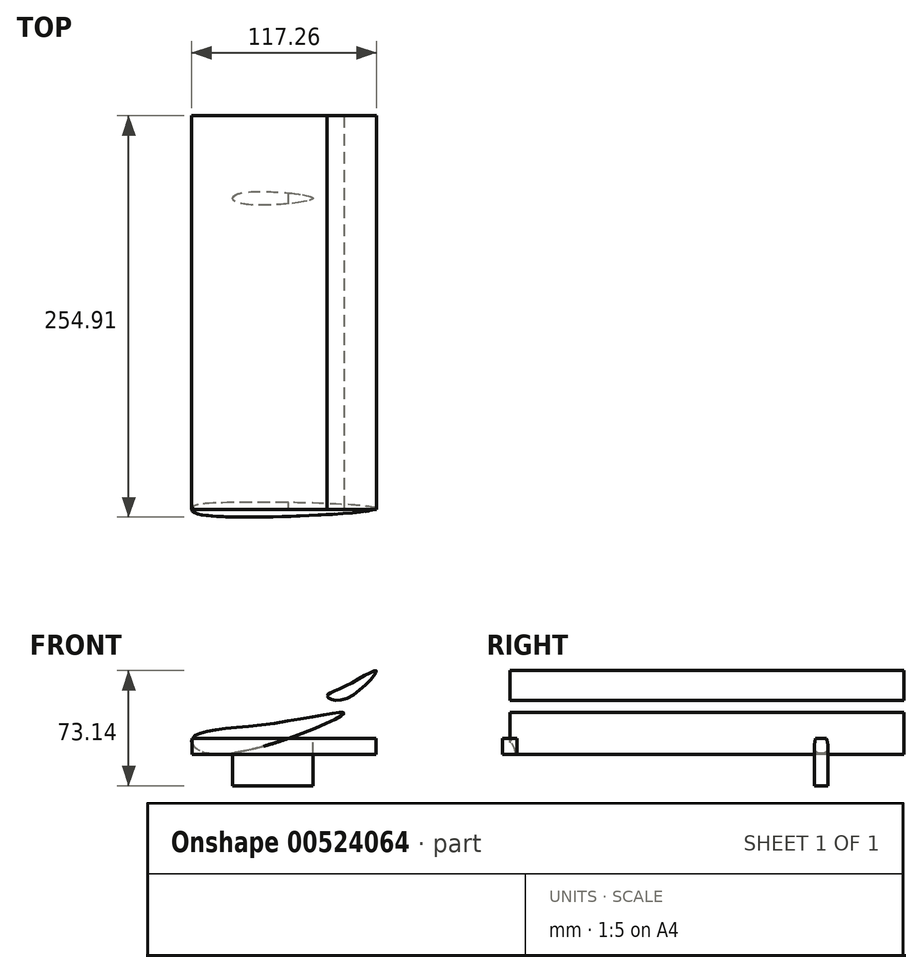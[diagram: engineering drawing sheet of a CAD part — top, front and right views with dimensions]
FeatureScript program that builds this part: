
annotation { "Feature Type Name" : "Feature", "Feature Type Description" : "" }
export const myFeature = defineFeature(function(context is Context, id is Id, definition is map)
    precondition{}
    {
        {
            var Q0;
            Q0=qCreatedBy(makeId("Front.planeOp"),FACE);
            var sketch = newSketch(context, id + "F0", { "sketchPlane" : qUnion([Q0])});
            skFitSpline(sketch, "E0", {"points": [v(-50.29, 0) * mm, v(-37.55, -9.85) * mm, v(45.9, 15.64) * mm, v(0, 9.49) * mm, v(-50.29, 0) * mm]});
            skFitSpline(sketch, "E1", {"points": [v(35.36, 27.07) * mm, v(45.9, 24.87) * mm, v(66.54, 42.89) * mm, v(45.9, 32.78) * mm, v(35.36, 27.07) * mm]});
            skSolve(sketch);
        }
        {
            var Q0;
            Q0 = qSketchRegion(id + "F0", true);
            extrude(context, id + "F1", {"entities" : qUnion([Q0]), "depth" : 250 * mm, "offsetDistance" : 25.4 * mm});
        }
        {
            var Q0;
            Q0=qCreatedBy(makeId("Top.planeOp"),FACE);
            var sketch = newSketch(context, id + "F2", { "sketchPlane" : qUnion([Q0])});
            skFitSpline(sketch, "E2", {"points": [v(-50.61, -249.52) * mm, v(-45.35, -253.24) * mm, v(66.49, -249.52) * mm, v(-45.04, -246.73) * mm, v(-50.61, -249.52) * mm]});
            skSolve(sketch);
        }
        {
            var Q0;
            Q0=sQuery(id+"F2.wireOp",EDGE,"E2");
            extrude(context, id + "F3", {"bodyType" : ToolBodyType.SURFACE, "surfaceEntities" : qUnion([Q0]), "depth" : 50 * mm, "offsetDistance" : 25.4 * mm});
        }
        {
            var Q0;
            Q0=makeQuery(id+"F2.imprint","IMPRINT",FACE,{"disambiguationData":[TD([[makeQuery(id+"F2.imprint","IMPRINT",EDGE,{"derivedFrom":sQuery(id+"F2.wireOp",EDGE,"E2")}),1.0]])]});
            var Q1;
            Q1=sQuery(id+"F2.wireOp",EDGE,"E2");
            extrude(context, id + "F4", {"entities" : qUnion([Q0]), "operationType" : NewBodyOperationType.ADD, "surfaceEntities" : qUnion([Q1]), "oppositeDirection" : true, "depth" : 10 * mm, "offsetDistance" : 25.4 * mm});
        }
        {
            var Q0;
            Q0=sQuery(id+"F2.wireOp",EDGE,"E2");
            extrude(context, id + "F5", {"bodyType" : ToolBodyType.SURFACE, "surfaceEntities" : qUnion([Q0]), "oppositeDirection" : true, "depth" : 10.83 * mm, "offsetDistance" : 25.4 * mm});
        }
        {
            var Q0;
            Q0=qCreatedBy(makeId("Top.planeOp"),FACE);
            var sketch = newSketch(context, id + "F6", { "sketchPlane" : qUnion([Q0])});
            skFitSpline(sketch, "E3", {"points": [v(-24.82, -52.46) * mm, v(-16.47, -48.56) * mm, v(26.4, -52.46) * mm, v(-15.91, -56.36) * mm, v(-24.82, -52.46) * mm]});
            skSolve(sketch);
        }
        {
            var Q0;
            Q0 = qSketchRegion(id + "F6", true);
            extrude(context, id + "F7", {"entities" : qUnion([Q0]), "operationType" : NewBodyOperationType.ADD, "oppositeDirection" : true, "depth" : 30 * mm, "offsetDistance" : 25.4 * mm});
        }
    });
